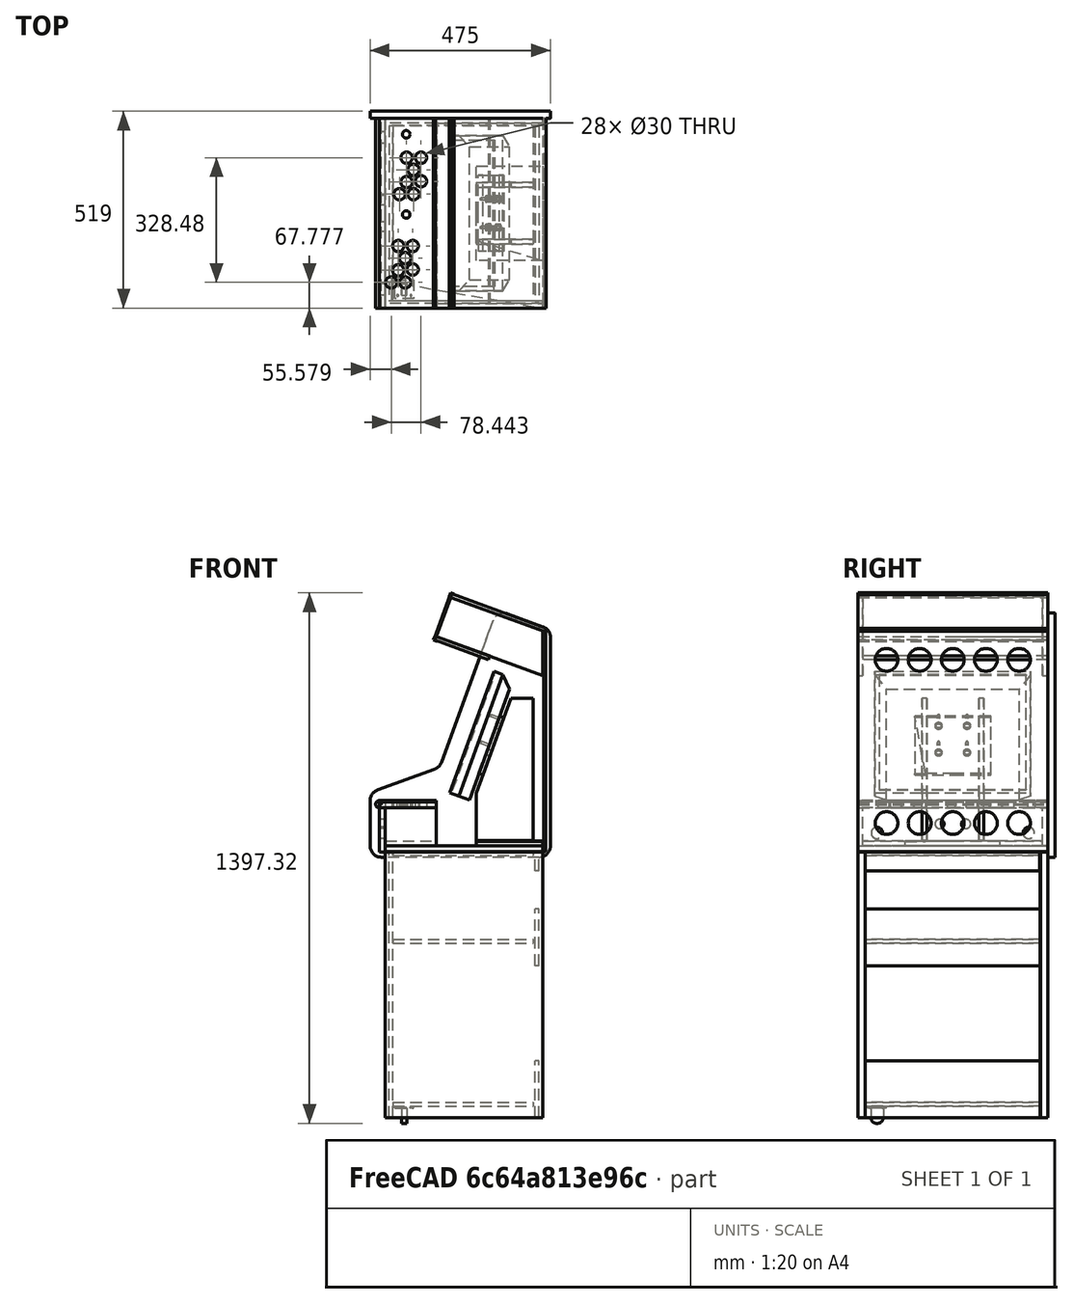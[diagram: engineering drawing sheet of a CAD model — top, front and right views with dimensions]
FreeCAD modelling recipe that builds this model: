
FCSTD DOCUMENT  (FreeCAD 0.18R16131 (Git))
Label: 600_ASM_Cabinet_NoMarquee
License: All rights reserved
LicenseURL: http://en.wikipedia.org/wiki/All_rights_reserved
objects: TechDraw::DrawViewDimension×8, Part::FeaturePython×3, Spreadsheet::Sheet×1, Sketcher::SketchObject×1, TechDraw::DrawSVGTemplate×1, TechDraw::DrawViewPart×1, TechDraw::DrawPage×1, App::DocumentObjectGroup×1
note: 4 computed .brp shape members not serialized (recipe doc carries the construction recipe); baked Part::Feature solids carry a one-line shape summary decoded from their .brp

FEATURE [Spreadsheet::Sheet] Spreadsheet  label="XLS"
  cells = B2=BODY FLOOR; E2=Ext.Ref; B3=Z=; C3=16; D3=.T; E3=Thichness; B4=Y=; C4=500; D4=.W; E4=Width; B5=X=; C5=400; D5=.D; E5=Depth; B7=Position Side Wall; D8=Left; E8=Right; B9=X0; D9(X0)==+C5; B10=Y0; C10=Y0_2; D10(Y0)==+C4; E10(Y0_2)==+D10 - D11; B11=Z0; D11(Z0)=13; B15=Position Front Wall; B16=x; C16=X0_Front; D16(X0_Front)==+H16 * abs(cos(D19)); F16=Distance on incline; G16=nS; H16(nS)=50; I16=mm; B17=y; C17=Y0_Front; D17(Y0_Front)=0; B18=z; C18=Z0_Front; D18(Z0_Front)==+H16 * abs(sin(D19)) + H18 + H20; F18=Hight of Incline; G18=nH; H18(nH)==125 + 2; I18=mm; B19=angle; C19=angley; D19(angley)=-70; F20=Thickness Material; H20=13; B22=Position Pedastil; B23=x; C23=x_pedastil; D23(x_pedastil)=0; B24=y; C24=y_pedastil; D24(y_pedastil)=0; B25=z; C25=z_pedastil; D25(z_pedastil)=-716; B27=Position Marquee; B28=x; C28==x_pedastil; B29=y; C29==y_pedastil; B30=z; C30==z_pedastil; B31=Incline
FEATURE [Part::FeaturePython] _00_ASM_Marquee_001  label="700_ASM_Marquee_001"  # a2plus imported part (geometry in sourceFile) (typed FeaturePython)
  Placement = pos=(130.914,8.47e-13,541.848) rot=(0,1,0;0.349066rad)
  a2p_Version = V0.1
  fixedPosition = false
  sourceFile = ./700_ASM_Marquee.FCStd
  subassemblyImport = true
  timeLastImport = 1.59379e+09
  updateColors = true
FEATURE [Part::FeaturePython] _00_ASM_Pedastil_001  label="500_ASM_Pedastil_001"  # a2plus imported part (geometry in sourceFile) (typed FeaturePython)
  Placement = pos=(0,0,-716) rot=(0,0,1;0rad)
  a2p_Version = V0.1
  fixedPosition = false
  sourceFile = ./500_ASM_Pedastil.FCStd
  subassemblyImport = true
  timeLastImport = 1.5937e+09
  updateColors = true
  expr: Placement.Base.z = XLS.z_pedastil
  expr: Placement.Base.y = XLS.y_pedastil
  expr: Placement.Base.x = XLS.x_pedastil
FEATURE [Sketcher::SketchObject] Sketch
  MapMode = 2
  Placement = pos=(0,-16,-79) rot=(1,0,0;1.5708rad)
  Support = -> [Sketch]
  sketch-geometry (8):
    g0: LineSegment StartX=-19.8955 StartY=66.3303 StartZ=0 EndX=415.104 EndY=66.3303 EndZ=0
    g1: LineSegment StartX=415.104 StartY=66.3303 StartZ=0 EndX=415.104 EndY=656.33 EndZ=0
    g2: LineSegment StartX=415.104 StartY=656.33 StartZ=0 EndX=175.483 EndY=743.545 EndZ=0
    g3: LineSegment StartX=175.483 StartY=743.545 StartZ=0 EndX=131.02 EndY=621.385 EndZ=0
    g4: LineSegment StartX=131.02 StartY=621.385 StartZ=0 EndX=271.974 EndY=570.082 EndZ=0
    g5: LineSegment StartX=271.974 StartY=570.082 StartZ=0 EndX=135.94 EndY=196.33 EndZ=0
    g6: LineSegment StartX=135.94 StartY=196.33 StartZ=0 EndX=-19.8955 EndY=196.33 EndZ=0
    g7: LineSegment StartX=-19.8955 StartY=196.33 StartZ=0 EndX=-19.8955 EndY=66.3303 EndZ=0
  constraints (22):
    c: Coincident(g0,g1)
    c: Coincident(g1,g2)
    c: Coincident(g2,g3)
    c: Coincident(g3,g4)
    c: Coincident(g4,g5)
    c: Coincident(g5,g6)
    c: Coincident(g6,g7)
    c: Perpendicular(g6,g7)
    c: Vertical(g7)
    c: Angle(g5,g6) = 1.91986
    c: Vertical(g1)
    c: Distance(g2) = 255
    c: Distance(g4) = 150
    c: Distance(g3) = 130
    c: Coincident(g7,g0)
    c: Horizontal(g0)
    c: DistanceY(g7,g7) = 130
    c: Distance(g1) = 590
    c: DistanceX(g0,g0) = 435
    c: Angle(g2,g1) = 1.91986
    c: Perpendicular(g3,g4)
    c: Perpendicular(g3,g2)
FEATURE [TechDraw::DrawSVGTemplate] Template
  EditableTexts = Designed_by_Name=Designed by Name; Drawing_number=Drawing number; FC-Date=Date; FC-SC=Scale; FC-SH=Sheet; FC-Title=Title; Subtitle=Subtitle; Weight=Weight
  Height = 210
  Orientation = 1
  Width = 297
FEATURE [TechDraw::DrawViewPart] View
  CoarseView = false
  Direction = (0,1,0)
  Focus = 100
  HardHidden = false
  IsoCount = 0
  IsoHidden = false
  IsoVisible = false
  LockPosition = false
  Perspective = false
  Rotation = 0
  Scale = 0.2
  ScaleType = 2
  SeamHidden = false
  SeamVisible = false
  SmoothHidden = false
  SmoothVisible = false
  Source = -> [Sketch]
  X = 82.8834
  Y = 120.789
FEATURE [TechDraw::DrawViewDimension] Dimension
  Arbitrary = false
  FormatSpec = %.2f
  LockPosition = false
  MeasureType = 1
  OverTolerance = 0
  References2D = -> [View]
  Rotation = 0
  ScaleType = 0
  Type = 0
  UnderTolerance = 0
  X = 17.943
  Y = 58.2435
FEATURE [TechDraw::DrawViewDimension] Dimension001
  Arbitrary = false
  FormatSpec = %.2f
  LockPosition = false
  MeasureType = 1
  OverTolerance = 0
  References2D = -> [View]
  Rotation = 0
  ScaleType = 0
  Type = 0
  UnderTolerance = 0
  X = -19.586
  Y = 70.5624
FEATURE [TechDraw::DrawViewDimension] Dimension002
  Arbitrary = false
  FormatSpec = %.2f
  LockPosition = false
  MeasureType = 1
  OverTolerance = 0
  References2D = -> [View]
  Rotation = 0
  ScaleType = 0
  Type = 2
  UnderTolerance = 0
  X = -55.0858
  Y = -9.07825
FEATURE [TechDraw::DrawViewDimension] Dimension003
  Arbitrary = false
  FormatSpec = %.2f
  LockPosition = false
  MeasureType = 1
  OverTolerance = 0
  References2D = -> [View]
  Rotation = 0
  ScaleType = 0
  Type = 1
  UnderTolerance = 0
  X = 2.02342
  Y = -86
FEATURE [TechDraw::DrawViewDimension] Dimension004
  Arbitrary = false
  FormatSpec = %.2f
  LockPosition = false
  MeasureType = 1
  OverTolerance = 0
  References2D = -> [View]
  Rotation = 0
  ScaleType = 0
  Type = 2
  UnderTolerance = 0
  X = 47.8593
  Y = -53.922
FEATURE [TechDraw::DrawViewDimension] Dimension005
  Arbitrary = false
  FormatSpec = %.2f
  LockPosition = false
  MeasureType = 1
  OverTolerance = 0
  References2D = -> [View]
  Rotation = 0
  ScaleType = 0
  Type = 1
  UnderTolerance = 0
  X = 27.5479
  Y = -24.4456
FEATURE [TechDraw::DrawViewDimension] Dimension006
  Arbitrary = false
  FormatSpec = %.2f
  LockPosition = false
  MeasureType = 1
  OverTolerance = 0
  References2D = -> [View]
  Rotation = 0
  ScaleType = 0
  Type = 0
  UnderTolerance = 0
  X = -3.3933
  Y = 49.4045
FEATURE [TechDraw::DrawViewDimension] Dimension007
  Arbitrary = false
  FormatSpec = %.2f
  LockPosition = false
  MeasureType = 1
  OverTolerance = 0
  References2D = -> [View]
  Rotation = 0
  ScaleType = 0
  Type = 0
  UnderTolerance = 0
  X = -12.7963
  Y = -7.40136
FEATURE [TechDraw::DrawPage] Page
  KeepUpdated = true
  ProjectionType = 0
  Template = -> Template
  Views = -> [View,Dimension,Dimension001,Dimension002,Dimension003,Dimension004,Dimension005,Dimension006,Dimension007]
FEATURE [App::DocumentObjectGroup] Group
  Group = -> [Sketch,Page]
FEATURE [Part::FeaturePython] b_700_ASM_Cabinet_BarTop_001_  label="700_ASM_Cabinet_BarTop_001"  # a2plus imported part (geometry in sourceFile) (typed FeaturePython)
  a2p_Version = V0.1
  fixedPosition = false
  sourceFile = .\700_ASM_Cabinet_BarTop.FCStd
  subassemblyImport = true
  timeLastImport = 1.59439e+09
  updateColors = true
